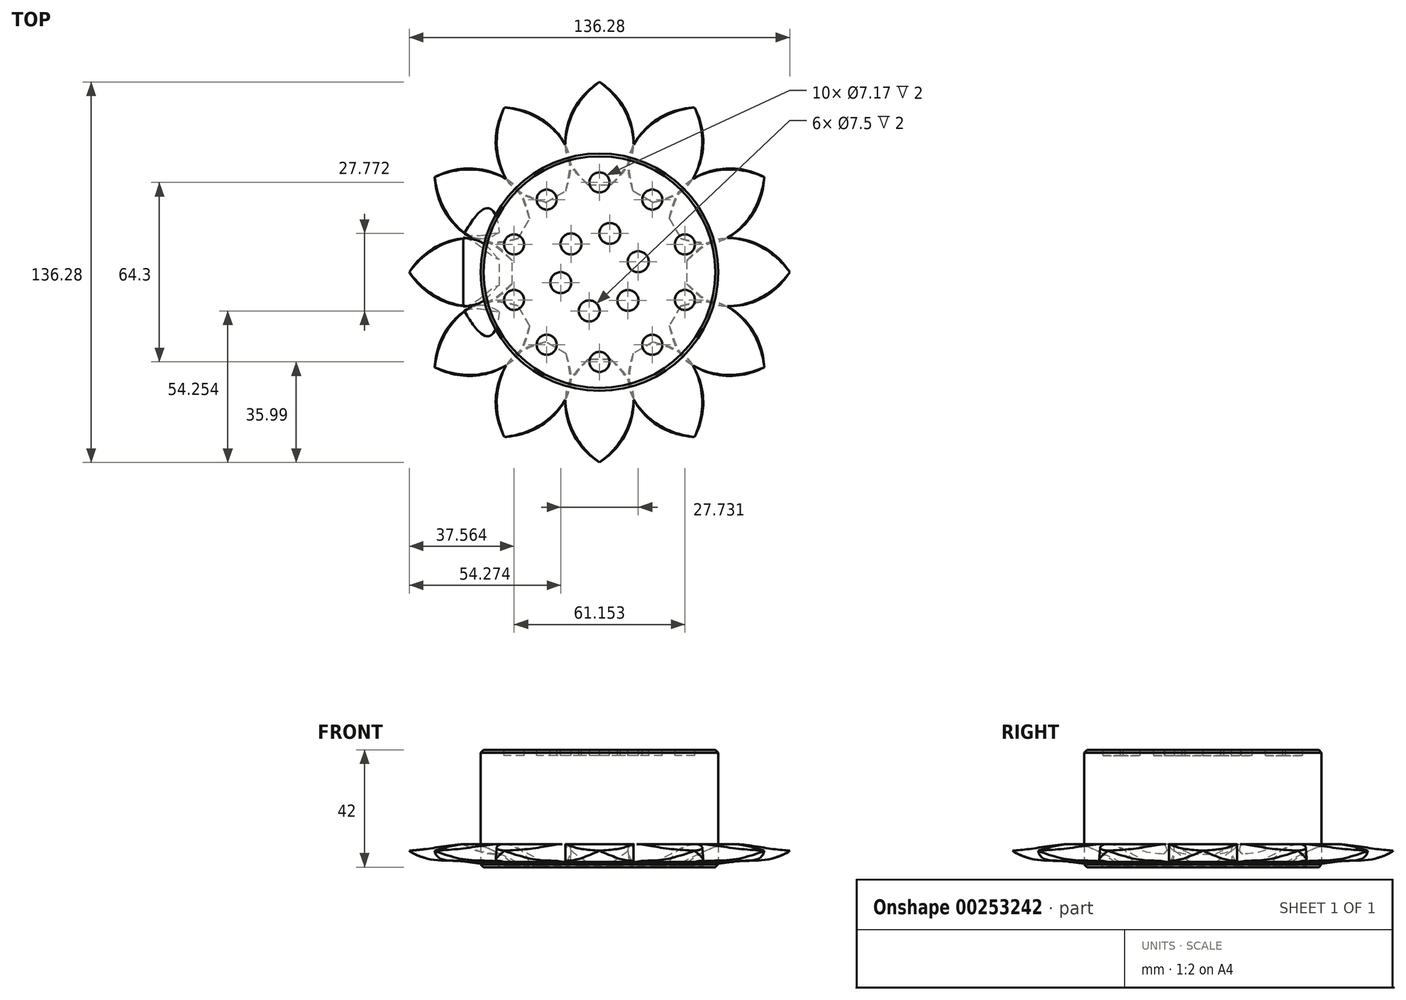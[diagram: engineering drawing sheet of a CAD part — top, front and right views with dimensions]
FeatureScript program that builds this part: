
annotation { "Feature Type Name" : "Feature", "Feature Type Description" : "" }
export const myFeature = defineFeature(function(context is Context, id is Id, definition is map)
    precondition{}
    {
        {
            var Q0;
            Q0=qCreatedBy(makeId("Top.planeOp"),FACE);
            var sketch = newSketch(context, id + "F0", { "sketchPlane" : qUnion([Q0])});
            skCircle(sketch, "E0", {"center": v(0, 0) * mm, "radius": 42.5 * mm});
            skPoint(sketch, "E1", {"position": v(0, 42.5) * mm});
            skPoint(sketch, "E2", {"position": v(0, -42.5) * mm});
            skPoint(sketch, "E3", {"position": v(42.5, 0) * mm});
            skPoint(sketch, "E4", {"position": v(-42.5, 0) * mm});
            skSolve(sketch);
        }
        {
            var Q0;
            Q0=qCreatedBy(makeId("Front.planeOp"),FACE);
            var sketch = newSketch(context, id + "F1", { "sketchPlane" : qUnion([Q0])});
            skFitSpline(sketch, "E5", {"points": [v(0, 28.6) * mm, v(-12, 0.76) * mm, v(-4.69, -6.5) * mm, v(0, -7.46) * mm], "startDerivative": vector(-44.82, -45.91) * mm, "endDerivative": vector(99.16, 0.35) * mm});
            skLineSegment(sketch, "E6", {"start": v(0, 28.6) * mm, "end": v(0, -7.46) * mm});
            skFitSpline(sketch, "E7.MirrorCS", {"points": [v(0, 28.6) * mm, v(12, 0.76) * mm, v(4.69, -6.5) * mm, v(0, -7.46) * mm], "startDerivative": vector(44.82, -45.91) * mm, "endDerivative": vector(-99.16, 0.35) * mm});
            skSolve(sketch);
        }
        {
            var Q0;
            Q0=qCreatedBy(makeId("Right.planeOp"),FACE);
            var sketch = newSketch(context, id + "F2", { "sketchPlane" : qUnion([Q0])});
            skLineSegment(sketch, "E8", {"start": v(-49.94, 12.5) * mm, "end": v(-38.32, -7.63) * mm});
            skSolve(sketch);
        }
        {
            var Q0;
            Q0=sQuery(id+"F2.wireOp",EDGE,"E8");
            cPlane(context, id + "F3", {"entities" : qUnion([Q0]), "cplaneType" : CPlaneType.LINE_ANGLE, "offset" : 25 * mm, "angle" : 90 * degree, "width" : 150 * mm, "height" : 150 * mm});
        }
        {
            var Q0;
            Q0=qCreatedBy(id+"F3.planeOp",FACE);
            var sketch = newSketch(context, id + "F4", { "sketchPlane" : qUnion([Q0])});
            skFitSpline(sketch, "E9", {"points": [v(0, 54.36) * mm, v(9.54, 39.14) * mm, v(12.73, 27.15) * mm, v(11.98, 22.23) * mm, v(9.9, 18.73) * mm, v(5.39, 14.95) * mm, v(4.63, 13.83) * mm, v(4.88, 13.25) * mm, v(3.37, 12.8) * mm, v(0, 12.77) * mm], "startDerivative": vector(51.68, -63.3) * mm, "endDerivative": vector(-33.57, 0.03) * mm});
            skFitSpline(sketch, "E10.MirrorCS", {"points": [v(0, 54.36) * mm, v(-9.54, 39.14) * mm, v(-12.73, 27.15) * mm, v(-11.98, 22.23) * mm, v(-9.9, 18.73) * mm, v(-5.39, 14.95) * mm, v(-4.63, 13.83) * mm, v(-4.88, 13.25) * mm, v(-3.37, 12.8) * mm, v(0, 12.77) * mm], "startDerivative": vector(-51.68, -63.3) * mm, "endDerivative": vector(33.57, 0.03) * mm});
            skSolve(sketch);
        }
        {
            var Q0;
            Q0=qCreatedBy(makeId("Right.planeOp"),FACE);
            var sketch = newSketch(context, id + "F5", { "sketchPlane" : qUnion([Q0])});
            skLineSegment(sketch, "E11", {"start": v(-31.2, -3.3) * mm, "end": v(-42.75, -9.96) * mm});
            skLineSegment(sketch, "E12", {"start": v(-34.1, -4.96) * mm, "end": v(-42.75, -9.96) * mm, "construction": true});
            skLineSegment(sketch, "E13", {"start": v(-33.45, -5.43) * mm, "end": v(-38.14, -10.06) * mm, "construction": true});
            skFitSpline(sketch, "E14.0", {"points": [v(-51.08, 44.83) * mm, v(-50.6, 42.37) * mm, v(-49.83, 38.35) * mm, v(-48.88, 33.41) * mm, v(-48.33, 30.57) * mm, v(-47.79, 27.72) * mm, v(-47.25, 24.92) * mm, v(-46.74, 22.29) * mm, v(-46.38, 20.43) * mm, v(-46.05, 18.72) * mm, v(-45.76, 17.2) * mm, v(-45.5, 15.85) * mm, v(-45.2, 14.24) * mm, v(-44.92, 12.84) * mm, v(-44.67, 11.53) * mm, v(-44.48, 10.56) * mm, v(-44.3, 9.6) * mm, v(-44.1, 8.61) * mm, v(-43.93, 7.67) * mm, v(-43.76, 6.8) * mm, v(-43.62, 6.06) * mm, v(-43.5, 5.48) * mm, v(-43.41, 5) * mm, v(-43.33, 4.55) * mm, v(-43.27, 4.24) * mm, v(-43.23, 4.06) * mm, v(-43.22, 3.98) * mm, v(-43.22, 3.97) * mm, v(-43.22, 3.97) * mm], "construction": true});
            skLineSegment(sketch, "E15", {"start": v(-32.96, -5.7) * mm, "end": v(-35.56, -10.33) * mm, "construction": true});
            skLineSegment(sketch, "E16.0", {"start": v(-49.17, 34.69) * mm, "end": v(-65.44, 24.45) * mm, "construction": true});
            skFitSpline(sketch, "E17.0", {"points": [v(-65.85, 25.2) * mm, v(-64.52, 23.07) * mm, v(-62.36, 19.6) * mm, v(-59.7, 15.34) * mm, v(-58.16, 12.88) * mm, v(-56.63, 10.42) * mm, v(-55.12, 8) * mm, v(-53.7, 5.72) * mm, v(-52.7, 4.12) * mm, v(-51.78, 2.64) * mm, v(-50.95, 1.33) * mm, v(-50.23, 0.17) * mm, v(-49.36, -1.23) * mm, v(-48.6, -2.44) * mm, v(-47.9, -3.57) * mm, v(-47.38, -4.4) * mm, v(-46.85, -5.24) * mm, v(-46.33, -6.1) * mm, v(-45.82, -6.9) * mm, v(-45.35, -7.66) * mm, v(-44.95, -8.3) * mm, v(-44.64, -8.8) * mm, v(-44.38, -9.21) * mm, v(-44.14, -9.6) * mm, v(-43.97, -9.87) * mm, v(-43.87, -10.02) * mm, v(-43.83, -10.1) * mm, v(-43.82, -10.1) * mm, v(-43.82, -10.1) * mm], "construction": true});
            skLineSegment(sketch, "E18", {"start": v(-33.45, -5.43) * mm, "end": v(-39.5, -11.4) * mm, "construction": true});
            skFitSpline(sketch, "E19", {"points": [v(-31.2, -3.3) * mm, v(-43.26, 3.94) * mm, v(-65.44, 24.45) * mm, v(-50.18, 0) * mm, v(-32, -4) * mm, v(-31.2, -3.3) * mm]});
            skSolve(sketch);
        }
        {
            var Q0;
            Q0=qCreatedBy(makeId("Front.planeOp"),FACE);
            var sketch = newSketch(context, id + "F6", { "sketchPlane" : qUnion([Q0])});
            skLineSegment(sketch, "E20", {"start": v(-36.62, -6.4) * mm, "end": v(-58.45, -2.8) * mm});
            skSolve(sketch);
        }
        {
            var Q0;
            Q0=sQuery(id+"F6.wireOp",EDGE,"E20");
            cPlane(context, id + "F7", {"entities" : qUnion([Q0]), "cplaneType" : CPlaneType.LINE_ANGLE, "offset" : 25 * mm, "angle" : 90 * degree, "width" : 150 * mm, "height" : 150 * mm});
        }
        {
            var Q0;
            Q0=qCreatedBy(id+"F7.planeOp",FACE);
            var sketch = newSketch(context, id + "F8", { "sketchPlane" : qUnion([Q0])});
            skFitSpline(sketch, "E21", {"points": [v(-66.7, 0) * mm, v(-54.9, 10) * mm, v(-40.32, 11.57) * mm, v(-29.48, 4.1) * mm], "startDerivative": vector(26.15, 36.68) * mm, "endDerivative": vector(31.34, -29.85) * mm});
            skLineSegment(sketch, "E22", {"start": v(-29.48, 4.1) * mm, "end": v(-29.48, 0) * mm});
            skFitSpline(sketch, "E23.MirrorCS", {"points": [v(-66.7, 0) * mm, v(-54.9, -10) * mm, v(-40.32, -11.57) * mm, v(-29.48, -4.1) * mm], "startDerivative": vector(26.15, -36.68) * mm, "endDerivative": vector(31.34, 29.85) * mm});
            skLineSegment(sketch, "E24.MirrorCS", {"start": v(-29.48, -4.1) * mm, "end": v(-29.48, 0) * mm});
            skSolve(sketch);
        }
        {
            var Q0;
            Q0=qCreatedBy(makeId("Front.planeOp"),FACE);
            var sketch = newSketch(context, id + "F9", { "sketchPlane" : qUnion([Q0])});
            skFitSpline(sketch, "E25.0.2", {"points": [v(-60.92, -11.54) * mm, v(-58.33, -10.02) * mm, v(-51.55, -6.03) * mm, v(-37.57, 2.2) * mm, v(-31.72, 5.63) * mm, v(-28.85, 7.32) * mm], "construction": true});
            skFitSpline(sketch, "E26", {"points": [v(-31.27, -7.7) * mm, v(-40.4, -2.27) * mm, v(-54.16, -1.52) * mm, v(-68.15, -3.29) * mm], "startDerivative": vector(-4.17, 4.16) * mm, "endDerivative": vector(-36.33, -1.6) * mm});
            skFitSpline(sketch, "E27", {"points": [v(-31.28, -7.7) * mm, v(-31.28, -8.4) * mm, v(-34.8, -8.68) * mm, v(-47.52, -7.3) * mm, v(-47.54, -7.3) * mm, v(-49.53, -7.1) * mm, v(-57.32, -6.76) * mm, v(-62.87, -5.82) * mm, v(-68.15, -3.29) * mm], "startDerivative": vector(2.71, -12.84) * mm, "endDerivative": vector(-13.17, 14.18) * mm});
            skSolve(sketch);
        }
        {
            var Q0;
            Q0=makeQuery(id+"F4.imprint","IMPRINT",FACE,{"disambiguationData":[TD([[makeQuery(id+"F4.imprint","IMPRINT",EDGE,{"derivedFrom":sQuery(id+"F4.wireOp",EDGE,"E9")}),-1.0]])]});
            extrude(context, id + "F10", {"entities" : qUnion([Q0]), "depth" : 10 * mm, "hasSecondDirection" : true, "secondDirectionOppositeDirection" : true, "secondDirectionDepth" : 10 * mm});
        }
        {
            var Q0;
            Q0 = qSketchRegion(id + "F5", true);
            extrude(context, id + "F11", {"entities" : qUnion([Q0]), "operationType" : NewBodyOperationType.INTERSECT, "endBound" : BoundingType.THROUGH_ALL, "depth" : 25 * mm, "hasSecondDirection" : true, "secondDirectionBound" : SecondDirectionBoundingType.THROUGH_ALL, "secondDirectionOppositeDirection" : true, "secondDirectionDepth" : 25 * mm});
        }
        {
            var Q0;
            Q0=makeQuery(id+"F10.opExtrude","SWEPT_BODY",BODY,{"disambiguationData":[OSD([sQuery(id+"F4.wireOp",EDGE,"E9"),sQuery(id+"F4.wireOp",EDGE,"E10.MirrorCS")])]});
            var Q1;
            Q1=sQuery(id+"F0.wireOp",EDGE,"E0");
            circularPattern(context, id + "F12", {"entities" : qUnion([Q0]), "axis" : qUnion([Q1]), "angle" : 360 * degree, "instanceCount" : 12, "equalSpace" : true});
        }
        {
            var Q0;
            Q0=makeQuery(id+"F8.imprint","IMPRINT",FACE,{"disambiguationData":[TD([[makeQuery(id+"F8.imprint","IMPRINT",EDGE,{"derivedFrom":sQuery(id+"F8.wireOp",EDGE,"E21")}),-1.0]])]});
            extrude(context, id + "F13", {"entities" : qUnion([Q0]), "depth" : 4 * mm, "hasSecondDirection" : true, "secondDirectionOppositeDirection" : true, "secondDirectionDepth" : 5.8 * mm});
        }
        {
            var Q0;
            Q0 = qSketchRegion(id + "F9", true);
            extrude(context, id + "F14", {"entities" : qUnion([Q0]), "operationType" : NewBodyOperationType.INTERSECT, "endBound" : BoundingType.THROUGH_ALL, "depth" : 25 * mm, "hasSecondDirection" : true, "secondDirectionBound" : SecondDirectionBoundingType.THROUGH_ALL, "secondDirectionOppositeDirection" : true, "secondDirectionDepth" : 25 * mm});
        }
        {
            var Q0;
            Q0=makeQuery(id+"F13.opExtrude","SWEPT_BODY",BODY,{"disambiguationData":[OSD([sQuery(id+"F8.wireOp",EDGE,"E21"),sQuery(id+"F8.wireOp",EDGE,"E22"),sQuery(id+"F8.wireOp",EDGE,"E23.MirrorCS"),sQuery(id+"F8.wireOp",EDGE,"E24.MirrorCS")])]});
            var Q1;
            Q1=sQuery(id+"F0.wireOp",EDGE,"E0");
            circularPattern(context, id + "F15", {"entities" : qUnion([Q0]), "axis" : qUnion([Q1]), "angle" : 360 * degree, "instanceCount" : 12, "equalSpace" : true});
        }
        {
            var Q0;
            Q0 = qSketchRegion(id + "F0", true);
            extrude(context, id + "F16", {"entities" : qUnion([Q0]), "depth" : 32.8 * mm, "hasSecondDirection" : true, "secondDirectionOppositeDirection" : true, "secondDirectionDepth" : 9.2 * mm});
        }
        {
            var Q0;
            Q0=makeQuery(id+"F16.opExtrude","CAP_FACE",FACE,{"disambiguationData":[OSD([sQuery(id+"F0.wireOp",EDGE,"E0")])],"isStart":false});
            cPlane(context, id + "F17", {"entities" : qUnion([Q0]), "cplaneType" : CPlaneType.OFFSET, "offset" : 0 * mm, "width" : 150 * mm, "height" : 150 * mm});
        }
        {
            var Q0;
            Q0=qCreatedBy(id+"F17.planeOp",FACE);
            var sketch = newSketch(context, id + "F18", { "sketchPlane" : qUnion([Q0])});
            skCircle(sketch, "E28", {"center": v(0, 32.15) * mm, "radius": 3.58 * mm});
            skCircle(sketch, "E29.1.0", {"center": v(-18.9, 26) * mm, "radius": 3.58 * mm});
            skCircle(sketch, "E29.2.0", {"center": v(-30.58, 9.93) * mm, "radius": 3.58 * mm});
            skCircle(sketch, "E29.3.0", {"center": v(-30.58, -9.93) * mm, "radius": 3.58 * mm});
            skCircle(sketch, "E29.4.0", {"center": v(-18.9, -26) * mm, "radius": 3.58 * mm});
            skCircle(sketch, "E29.5.0", {"center": v(0, -32.15) * mm, "radius": 3.58 * mm});
            skCircle(sketch, "E29.6.0", {"center": v(18.9, -26) * mm, "radius": 3.58 * mm});
            skCircle(sketch, "E29.7.0", {"center": v(30.58, -9.93) * mm, "radius": 3.58 * mm});
            skCircle(sketch, "E29.8.0", {"center": v(30.58, 9.93) * mm, "radius": 3.58 * mm});
            skCircle(sketch, "E29.9.0", {"center": v(18.9, 26) * mm, "radius": 3.58 * mm});
            skPoint(sketch, "E29.center", {"position": v(0, 0) * mm});
            skCircle(sketch, "E30", {"center": v(-10.19, 10.13) * mm, "radius": 3.75 * mm});
            skCircle(sketch, "E31.1.0", {"center": v(-13.87, -3.76) * mm, "radius": 3.75 * mm});
            skCircle(sketch, "E31.2.0", {"center": v(-3.68, -13.89) * mm, "radius": 3.75 * mm});
            skCircle(sketch, "E31.3.0", {"center": v(10.19, -10.13) * mm, "radius": 3.75 * mm});
            skCircle(sketch, "E31.4.0", {"center": v(13.87, 3.76) * mm, "radius": 3.75 * mm});
            skCircle(sketch, "E31.5.0", {"center": v(3.68, 13.89) * mm, "radius": 3.75 * mm});
            skSolve(sketch);
        }
        {
            var Q0;
            Q0 = qSketchRegion(id + "F18", true);
            extrude(context, id + "F19", {"entities" : qUnion([Q0]), "operationType" : NewBodyOperationType.REMOVE, "oppositeDirection" : true, "depth" : 2 * mm});
        }
        {
            var Q0;
            Q0=makeQuery(id+"F16.opExtrude","CAP_EDGE",EDGE,{"disambiguationData":[OSD([sQuery(id+"F0.wireOp",EDGE,"E0")])],"isStart":false});
            chamfer(context, id + "F20", {"entities" : qUnion([Q0]), "width" : 1 * mm, "tangentPropagation" : true});
        }
        {
            var Q0;
            Q0=makeQuery(id+"F16.opExtrude","CAP_EDGE",EDGE,{"disambiguationData":[OSD([sQuery(id+"F0.wireOp",EDGE,"E0")])],"isStart":true});
            chamfer(context, id + "F21", {"entities" : qUnion([Q0]), "width" : 1 * mm, "tangentPropagation" : true});
        }
    });
